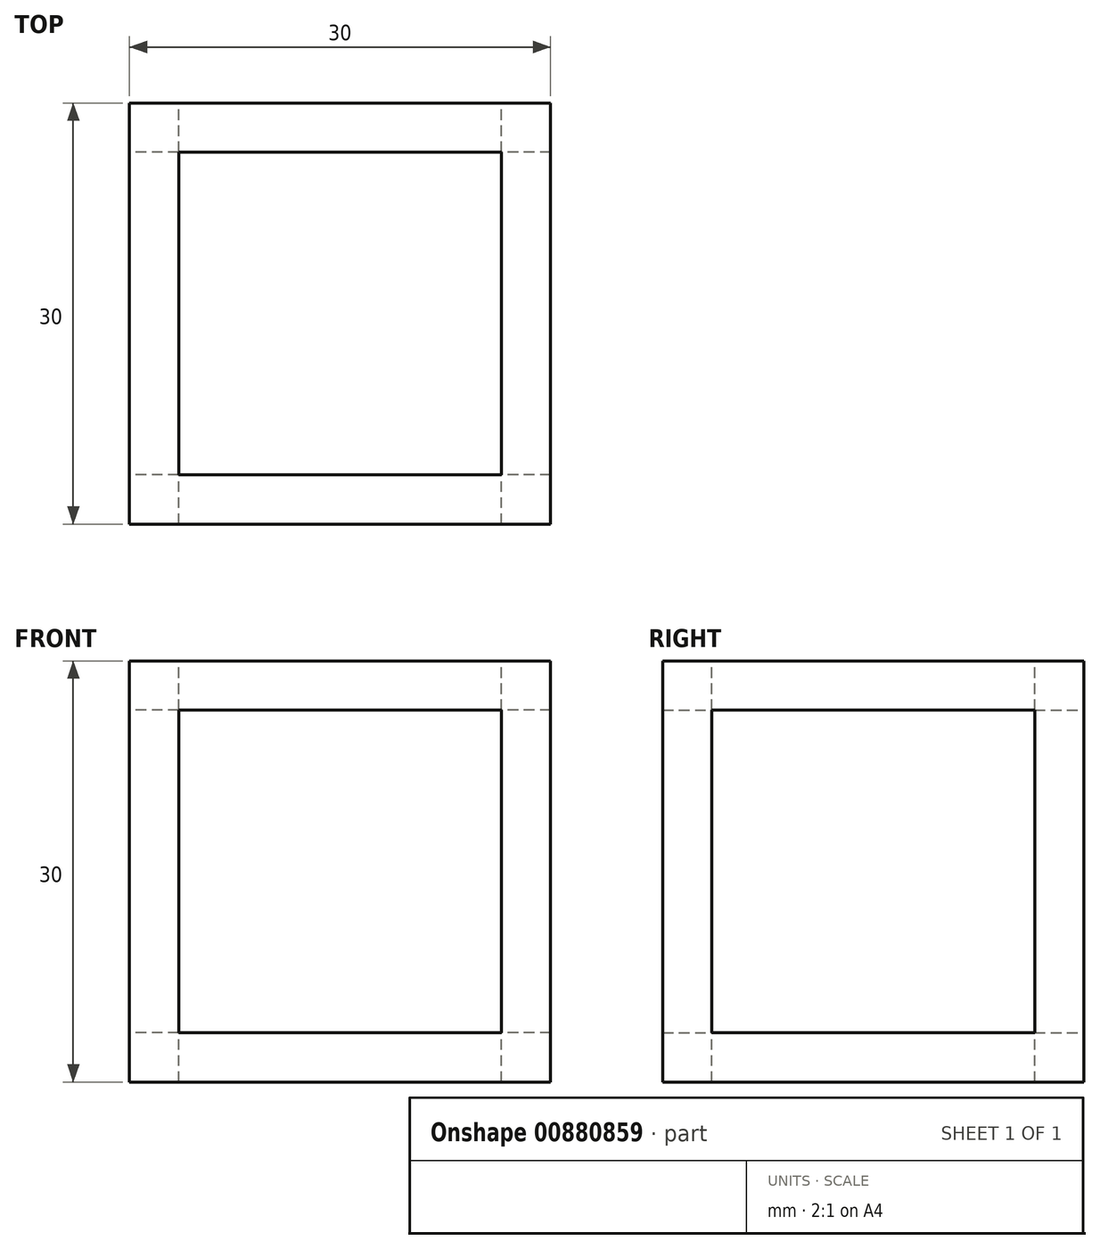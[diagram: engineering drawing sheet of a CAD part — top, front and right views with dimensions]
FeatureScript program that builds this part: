
annotation { "Feature Type Name" : "Feature", "Feature Type Description" : "" }
export const myFeature = defineFeature(function(context is Context, id is Id, definition is map)
    precondition{}
    {
        {
            var Q0;
            Q0=qCreatedBy(makeId("Front.planeOp"),FACE);
            var sketch = newSketch(context, id + "F0", { "sketchPlane" : qUnion([Q0])});
            skLineSegment(sketch, "E0.bottom", {"start": v(-15, 15) * mm, "end": v(15, 15) * mm});
            skLineSegment(sketch, "E0.top", {"start": v(-15, -15) * mm, "end": v(15, -15) * mm});
            skLineSegment(sketch, "E0.left", {"start": v(-15, 15) * mm, "end": v(-15, -15) * mm});
            skLineSegment(sketch, "E0.right", {"start": v(15, 15) * mm, "end": v(15, -15) * mm});
            skLineSegment(sketch, "E1", {"start": v(0, -15) * mm, "end": v(0, 15) * mm, "construction": true});
            skSolve(sketch);
        }
        {
            var Q0;
            Q0=makeQuery(id+"F0.imprint","IMPRINT",FACE,{"disambiguationData":[TD([[makeQuery(id+"F0.imprint","IMPRINT",EDGE,{"derivedFrom":sQuery(id+"F0.wireOp",EDGE,"E0.bottom")}),-1.0]])]});
            extrude(context, id + "F1", {"entities" : qUnion([Q0]), "depth" : 30 * mm, "offsetDistance" : 25 * mm});
        }
        {
            var Q0;
            Q0=makeQuery(id+"F1.opExtrude","CAP_FACE",FACE,{"disambiguationData":[OSD([sQuery(id+"F0.wireOp",EDGE,"E0.bottom"),sQuery(id+"F0.wireOp",EDGE,"E0.top"),sQuery(id+"F0.wireOp",EDGE,"E0.left"),sQuery(id+"F0.wireOp",EDGE,"E0.right")])],"isStart":true});
            var sketch = newSketch(context, id + "F2", { "sketchPlane" : qUnion([Q0])});
            skLineSegment(sketch, "E2.bottom", {"start": v(11.5, 11.5) * mm, "end": v(-11.5, 11.5) * mm});
            skLineSegment(sketch, "E2.top", {"start": v(11.5, -11.5) * mm, "end": v(-11.5, -11.5) * mm});
            skLineSegment(sketch, "E2.left", {"start": v(11.5, 11.5) * mm, "end": v(11.5, -11.5) * mm});
            skLineSegment(sketch, "E2.right", {"start": v(-11.5, 11.5) * mm, "end": v(-11.5, -11.5) * mm});
            skSolve(sketch);
        }
        {
            var Q0;
            Q0=makeQuery(id+"F2.imprint","IMPRINT",FACE,{"disambiguationData":[TD([[makeQuery(id+"F2.imprint","IMPRINT",EDGE,{"derivedFrom":sQuery(id+"F2.wireOp",EDGE,"E2.bottom")}),1.0]])]});
            extrude(context, id + "F3", {"entities" : qUnion([Q0]), "operationType" : NewBodyOperationType.REMOVE, "oppositeDirection" : true, "depth" : 30 * mm, "offsetDistance" : 25 * mm});
        }
        {
            var Q0;
            Q0=makeQuery(id+"F1.opExtrude","SWEPT_FACE",FACE,{"disambiguationData":[OSD([sQuery(id+"F0.wireOp",EDGE,"E0.left")])]});
            var sketch = newSketch(context, id + "F4", { "sketchPlane" : qUnion([Q0])});
            skLineSegment(sketch, "E3.bottom", {"start": v(3.5, 11.5) * mm, "end": v(26.5, 11.5) * mm});
            skLineSegment(sketch, "E3.top", {"start": v(3.5, -11.5) * mm, "end": v(26.5, -11.5) * mm});
            skLineSegment(sketch, "E3.left", {"start": v(3.5, 11.5) * mm, "end": v(3.5, -11.5) * mm});
            skLineSegment(sketch, "E3.right", {"start": v(26.5, 11.5) * mm, "end": v(26.5, -11.5) * mm});
            skSolve(sketch);
        }
        {
            var Q0;
            Q0=makeQuery(id+"F4.imprint","IMPRINT",FACE,{"disambiguationData":[TD([[makeQuery(id+"F4.imprint","IMPRINT",EDGE,{"derivedFrom":sQuery(id+"F4.wireOp",EDGE,"E3.bottom")}),-1.0]])]});
            extrude(context, id + "F5", {"entities" : qUnion([Q0]), "operationType" : NewBodyOperationType.REMOVE, "oppositeDirection" : true, "depth" : 30 * mm, "offsetDistance" : 25 * mm});
        }
        {
            var Q0;
            Q0=makeQuery(id+"F1.opExtrude","SWEPT_FACE",FACE,{"disambiguationData":[OSD([sQuery(id+"F0.wireOp",EDGE,"E0.bottom")])]});
            var sketch = newSketch(context, id + "F6", { "sketchPlane" : qUnion([Q0])});
            skLineSegment(sketch, "E4.bottom", {"start": v(-11.5, -3.5) * mm, "end": v(11.5, -3.5) * mm});
            skLineSegment(sketch, "E4.top", {"start": v(-11.5, -26.5) * mm, "end": v(11.5, -26.5) * mm});
            skLineSegment(sketch, "E4.left", {"start": v(-11.5, -3.5) * mm, "end": v(-11.5, -26.5) * mm});
            skLineSegment(sketch, "E4.right", {"start": v(11.5, -3.5) * mm, "end": v(11.5, -26.5) * mm});
            skSolve(sketch);
        }
        {
            var Q0;
            Q0=makeQuery(id+"F6.imprint","IMPRINT",FACE,{"disambiguationData":[TD([[makeQuery(id+"F6.imprint","IMPRINT",EDGE,{"derivedFrom":sQuery(id+"F6.wireOp",EDGE,"E4.bottom")}),-1.0]])]});
            extrude(context, id + "F7", {"entities" : qUnion([Q0]), "operationType" : NewBodyOperationType.REMOVE, "oppositeDirection" : true, "depth" : 30 * mm, "offsetDistance" : 25 * mm});
        }
    });
